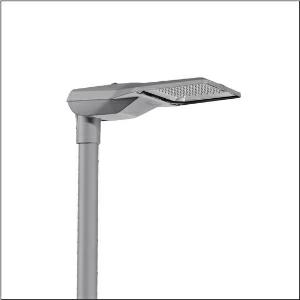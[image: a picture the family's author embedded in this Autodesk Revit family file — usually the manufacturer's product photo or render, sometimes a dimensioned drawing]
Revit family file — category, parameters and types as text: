
# Revit family: streetlight_sl_21_midi___stw1_0a_5xe3e33s08mb_c28b
name_source: partatom
category: Lighting Fixtures
units: mm (PartAtom-declared; Revit-internal decimal feet)

## family parameters
Cut with Voids When Loaded = No
Host = Face
Light Source = No
Part Type = Normal
Room Calculation Point = No
Round Connector Dimension = Use Diameter
Shared = No

## types (1)
- --- (1 x LED, 18270 lm, 136 W, 3000K)
    Apparent Load = 136 VA
    CIE Flux Codes = 38 75 98 100 100
    Color Rendering = 70
    Color Temperature = 3000K
    Default Elevation = 1800 mm
    Description = Streetlight SL 21 midi, mast luminaire, primary light control with lens, of PMMA, primary optical cover: cover, of toughened safety glass, transparent, light distribution: STW1.0a, light emission: direct distribution, primary light characteristic: asymmetric, installation type: side-entry, post-top, LED, High Power LED, rated luminous flux: 18.270lm, luminous efficacy: 134lm/W, light colour: 730, colour temperature: 3000K, control: overheat protection, constant luminous flux control, time-dependent luminous flux control, flexible luminous flux parameterisation, presetting dimming logarithmic, mains connection: 230..240V, AC, 50/60Hz, start of lifetime: 136W, end of service life: 142W, reduction: 61W, luminaire housing, of diecast aluminium, powder-coated, Siteco® metallic grey (DB 702S), corrosivity category C5 mid according to DIN EN ISO 12944, please order mast flange separately, inclination adjustable: 0°, 5°, 10°, 15°, sealing non-destructively replaceable, multi-level sealing system, length: 644mm, width: 335mm, height: 110mm, mast flange for spigot size: 42mm (side-entry): 5XC10008XM4, 60/48mm (side-entry/post-top): 5XC10108XM2, 76/60mm (side-entry/post-top): 5XC10108XM1, Smart Interface above, protection rating (complete): IP66, insulation class (complete): insulation class II (safety insulation), certification: CE, ENEC, ENEC+, VDE, impact resistance: IK09, permissible operating ambient temperature for outdoor applications: -40..+50°C, standard-compliant lighting for roads and squares, packaging unit: 1 piece

Light Distribution: STW1.0a
    Height = 111 mm
    Lamp = 1 x LED
    Lamp Light Flux = 18270 lm
    Lamp Power = 136 W
    Lamp count = 1
    Length = 644 mm
    Luminous efficacy = 134 lm/W
    Manufacturer = Siteco
    ModVariant = No
    Model = 5XE3E33S08MB
    Number of Poles = 1
    OnlyDefault = Yes
    Power Factor = 1
    Product Name = Streetlight SL 21 midi | STW1.0a
    Product group = mast luminaire | pylon top
    ProductGroupID = 6100
    Protection Class = Protection class II
    Protection Degree = IP 66
    RLX_Detail_Level = 1
    RLX_Emergency_Light_Flux = 0 lm
    RLX_Emergency_Type = 0
    RLX_Emergency_Type_DB = No
    RlxData = <blob elided: 90505 chars, md5=9d872f3c>
    Socket = socket
    Standby Power = 0 W
    System Light Flux = 18270 lm
    System Power = 136 W
    Type Comments = factory setting: luminous flux: 100 % | dim-lin: 254 | 695 mA
    Type Image = l_1004302.jpg
    URL = http://relux.com
    VarID = @adj_139967
    Voltage = 0 V
    Weight = 0.00 kg
    Width = 336 mm

## geometry (parser evidence)
native form markers: Blend x4, Sweep x12
no freeform markers — native parametric forms only
